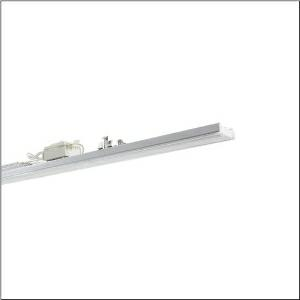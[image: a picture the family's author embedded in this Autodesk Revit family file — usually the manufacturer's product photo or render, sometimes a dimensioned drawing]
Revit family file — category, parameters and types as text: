
# Revit family: licross_11_recessed_mo_51tl19dn495g
name_source: partatom
category: Lighting Fixtures
units: mm (PartAtom-declared; Revit-internal decimal feet)

## family parameters
Cut with Voids When Loaded = No
Host = Face
Light Source = No
Part Type = Normal
Room Calculation Point = No
Round Connector Dimension = Use Diameter
Shared = No

## types (1)
- --- (1 x LED, 9810 lm, 56.7 W, 4000K)
    Apparent Load = 57 VA
    CIE Flux Codes = 55 90 98 100 100
    Color Rendering = 80
    Color Temperature = 4000K
    Default Elevation = 1800 mm
    Description = Licross 11 Recessed MO, luminaire insert, of sheet steel, coil coated, white, length: 1.500mm, width: 66mm, height: 67mm, LED rated luminous flux: 9.810lm, light colour: 840, SDCM (Standard Deviation of Colour Matching)MacAdam ≤ 2 SDCM (initial), control gear: DALI 2, with plug, 5-pole, with phase selection, mains connection: 220..240V, AC, 50/60Hz, rated input power: 57W, internal wiring halogen-free, primary light control with lens, of plastic, primary optical cover: cover, of PMMA, light emission: direct distribution, primary light characteristic: double asymmetric, protection rating (complete): IP40, insulation class (complete): insulation class I (protective earthing), certification: CE, ENEC, VDE, UKCA, protection symbol: D if used in an environment without relevant dust loads with corresponding accessories, impact resistance: IK06, permissible ambient temperature for indoor applications: -25..+35°C, corresponds to IFS (International Featured Standards) requirements for safety and quality in the food industry, reducing of maximum allowable ambient temperature of 5°C with ceiling mounting, LABS conformity tested according to VDMA 24364:2018-05, The light source and the operating device comply with the requirements of the Ecodesign Regulation (EU) 2019/2020 and are replaceable in accordance with this regulation, packaging unit: 1 piece
    Height = 58 mm
    Lamp = 1 x LED
    Lamp Light Flux = 9810 lm
    Lamp Power = 56.7 W
    Lamp count = 1
    Length = 1500 mm
    Luminous efficacy = 173 lm/W
    Manufacturer = Siteco
    ModVariant = No
    Model = 51TL19DN495G
    Mounting Place = Ceiling
    Mounting Type = Pendant
    Number of Poles = 1
    OnlyDefault = Yes
    Power Factor = 1
    Product Name = Licross 11 Recessed MO
    Product group = luminaire insert | ceiling pendant
    ProductGroupID = 901
    Protection Class = Protection class I
    Protection Degree = IP 40
    RLX_Detail_Level = 1
    RLX_Emergency_Light_Flux = 0 lm
    RLX_Emergency_Type = 0
    RLX_Emergency_Type_DB = No
    RlxData = <blob elided: 24749 chars, md5=82f6fb56>
    Socket = socket
    Standby Power = 0 W
    System Light Flux = 9810 lm
    System Power = 57 W
    Type Comments = factory setting: luminous flux: 100 % | dim-lin: 254 | 378 mA
    Type Image = l_1296930.jpg
    URL = http://relux.com
    VarID = @adj_102389
    Voltage = 0 V
    Weight = 0.00 kg
    Width = 66 mm

## geometry (parser evidence)
native form markers: Blend x4, Sweep x12
no freeform markers — native parametric forms only
